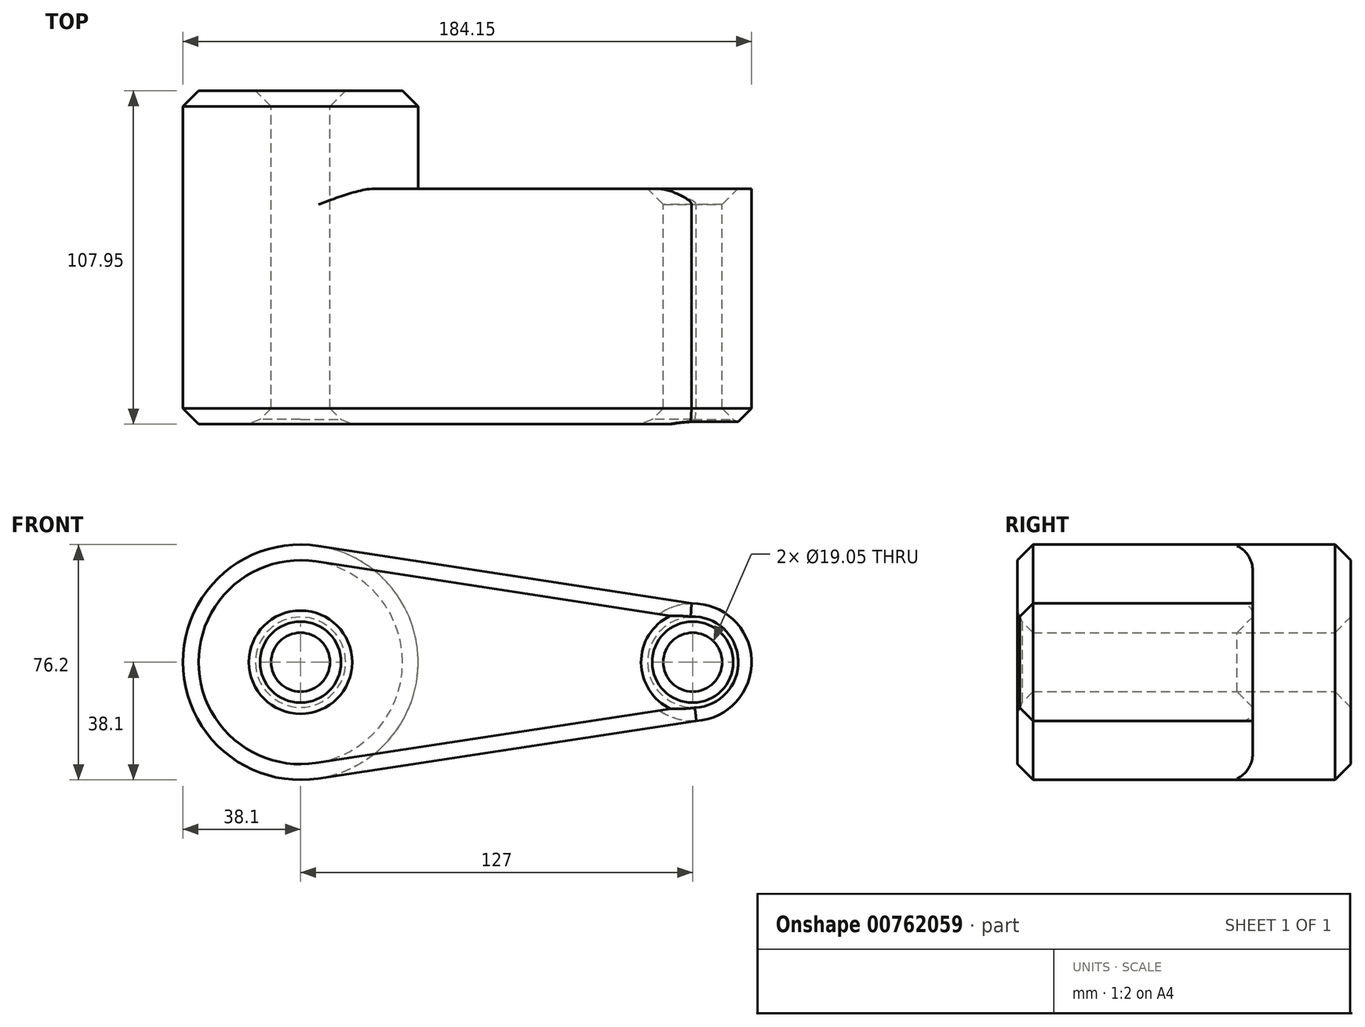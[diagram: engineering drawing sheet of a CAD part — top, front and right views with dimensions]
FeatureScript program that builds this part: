
annotation { "Feature Type Name" : "Feature", "Feature Type Description" : "" }
export const myFeature = defineFeature(function(context is Context, id is Id, definition is map)
    precondition{}
    {
        {
            var Q0;
            Q0=qCreatedBy(makeId("Front.planeOp"),FACE);
            var sketch = newSketch(context, id + "F0", { "sketchPlane" : qUnion([Q0])});
            skCircle(sketch, "E0", {"center": v(0, 0) * mm, "radius": 38.1 * mm});
            skCircle(sketch, "E1", {"center": v(127, 0) * mm, "radius": 19.05 * mm});
            skLineSegment(sketch, "E2", {"start": v(5.8, 37.66) * mm, "end": v(126.63, 19.05) * mm});
            skLineSegment(sketch, "E3", {"start": v(5.74, -37.67) * mm, "end": v(131.55, -18.5) * mm});
            skCircle(sketch, "E4", {"center": v(0, 0) * mm, "radius": 9.53 * mm});
            skCircle(sketch, "E5", {"center": v(127, 0) * mm, "radius": 9.53 * mm});
            skSolve(sketch);
        }
        {
            var Q0;
            Q0=qSketchRegion(id+"F0",true);
            extrude(context, id + "F1", {"entities" : qUnion([Q0]), "depth" : 76.2 * mm, "offsetDistance" : 25.4 * mm});
        }
        {
            var Q0;
            Q0=makeQuery(id+"F0.imprint","IMPRINT",FACE,{"disambiguationData":[TD([[makeQuery(id+"F0.imprint","IMPRINT",EDGE,{"derivedFrom":sQuery(id+"F0.wireOp",EDGE,"E4")}),-1.0]])]});
            extrude(context, id + "F2", {"entities" : qUnion([Q0]), "operationType" : NewBodyOperationType.ADD, "oppositeDirection" : true, "depth" : 31.75 * mm, "offsetDistance" : 25.4 * mm});
        }
        {
            var Q0;
            Q0=makeQuery(id+"F2.opExtrude","CAP_EDGE",EDGE,{"disambiguationData":[OSD([sQuery(id+"F0.wireOp",EDGE,"E4")])],"isStart":false});
            chamfer(context, id + "F3", {"entities" : qUnion([Q0]), "chamferType" : ChamferType.OFFSET_ANGLE, "width" : 5.08 * mm, "oppositeDirection" : false, "angle" : 45 * degree, "tangentPropagation" : true});
        }
        {
            var Q0;
            Q0=makeQuery(id+"F2.opExtrude","CAP_EDGE",EDGE,{"disambiguationData":[OSD([sQuery(id+"F0.wireOp",EDGE,"E0")])],"isStart":false});
            chamfer(context, id + "F4", {"entities" : qUnion([Q0]), "width" : 5.08 * mm, "tangentPropagation" : true});
        }
        {
            var Q0;
            Q0=makeQuery(id+"F1.opExtrude","CAP_EDGE",EDGE,{"disambiguationData":[OSD([sQuery(id+"F0.wireOp",EDGE,"E5")])],"isStart":true});
            chamfer(context, id + "F5", {"entities" : qUnion([Q0]), "width" : 5.08 * mm, "tangentPropagation" : true});
        }
        {
            var Q0;
            Q0=makeQuery(id+"F1.opExtrude","CAP_EDGE",EDGE,{"disambiguationData":[OSD([sQuery(id+"F0.wireOp",EDGE,"E4")])],"isStart":false});
            var Q1;
            Q1=makeQuery(id+"F1.opExtrude","CAP_EDGE",EDGE,{"disambiguationData":[OSD([sQuery(id+"F0.wireOp",EDGE,"E5")])],"isStart":false});
            chamfer(context, id + "F6", {"entities" : qUnion([Q0, Q1]), "width" : 5.08 * mm, "tangentPropagation" : true});
        }
        {
            var Q0;
            Q0=makeQuery(id+"F1.opExtrude","CAP_FACE",FACE,{"disambiguationData":[OSD([sQuery(id+"F0.wireOp",EDGE,"E0"),sQuery(id+"F0.wireOp",EDGE,"E1"),sQuery(id+"F0.wireOp",EDGE,"E2"),sQuery(id+"F0.wireOp",EDGE,"E3"),sQuery(id+"F0.wireOp",EDGE,"E4"),sQuery(id+"F0.wireOp",EDGE,"E5")])],"isStart":false});
            chamfer(context, id + "F7", {"entities" : qUnion([Q0]), "width" : 5.08 * mm, "tangentPropagation" : true});
        }
        {
            var Q0;
            Q0=makeQuery(id+"F1.opExtrude","CAP_EDGE",EDGE,{"disambiguationData":[OSD([sQuery(id+"F0.wireOp",EDGE,"E3")])],"isStart":true});
            fillet(context, id + "F8", {"entities" : qUnion([Q0]), "radius" : 5.08 * mm, "tangentPropagation" : true, "allowEdgeOverflow" : false});
        }
        {
            var Q0;
            Q0=makeQuery(id+"F1.opExtrude","CAP_EDGE",EDGE,{"disambiguationData":[OSD([sQuery(id+"F0.wireOp",EDGE,"E2")])],"isStart":true});
            fillet(context, id + "F9", {"entities" : qUnion([Q0]), "radius" : 5.08 * mm, "tangentPropagation" : true, "allowEdgeOverflow" : false});
        }
    });
